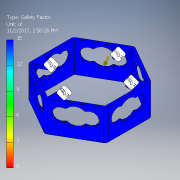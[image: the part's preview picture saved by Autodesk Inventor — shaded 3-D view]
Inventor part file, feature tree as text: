
AUTODESK INVENTOR PART (.ipt)
format: ipt  version: 2018 (Build 220112000, 112)  size: 514,048 bytes
history: native  units: mm
features: extrude x19, sketch x15, projected_geometry x14, fillet x2, hole x1, pattern_circular x1
ambient origin geometry x8: Origin, YZ Plane, XZ Plane, XY Plane, X Axis, Y Axis, Z Axis, Center Point
bodies: Solid1 (feature_tree)
feature tree (52):
  extrude  "Extrusion1"  Depth=3.0mm
  extrude  "Extrusion2"  Depth=37.0mm
  sketch  "Sketch5"  dims[d5=4.0mm d6=0.0mm d49=25.5mm]
  extrude  "Extrusion3"  Depth=4.0mm
  extrude  "Extrusion4"  Depth=11.7mm
  extrude  "Extrusion5"  Depth=23.0mm
  sketch  "Sketch9"  dims[d66=8.5mm d67=27.0mm]
  hole  "Hole3"  [1 undecoded]
  extrude  "Extrusion6"  Depth=27.0mm
  extrude  "Extrusion7"  Depth=22.0mm
  extrude  "Extrusion8"  Depth=13.0mm
  extrude  "Extrusion9"  Depth=14.5mm
  extrude  "Extrusion10"  Depth=54.864mm
  extrude  "Extrusion11"  Depth=4.5mm
  pattern_circular  "Circular Pattern1"  [2 undecoded]
  extrude  "Extrusion12"  Depth=22.0mm
  extrude  "Extrusion13"  Depth=22.0mm
  fillet  "Fillet1"  Radius=3.0mm
  fillet  "Fillet2"  Radius=3.0mm
  extrude  "Extrusion16"  Depth=3.0mm TaperAngle=0.0deg
  extrude  "Extrusion14"  Depth=3.0mm TaperAngle=0.0deg
  extrude  "Extrusion15"  Depth=3.0mm TaperAngle=0.0deg
  extrude  "Extrusion17"  Depth=3.0mm TaperAngle=0.0deg
  extrude  "Extrusion19"  Depth=4.0mm TaperAngle=360.0deg
  extrude  "Extrusion18"  Depth=10.0mm TaperAngle=0.0deg
  sketch  "Sketch1"  dims[d0=54.864mm d1=3.0mm]
  sketch  "Sketch2"  dims[d2=37.0mm d3=0.0mm d4=15.25mm]
  sketch  "Sketch6"  dims[d51=8.44mm d53=11.7mm]
  projected_geometry  "Projected Loop1"
  sketch  "Sketch7"  dims[d54=15.0mm d55=23.0mm]
  projected_geometry  "Projected Loop2"
  sketch  "Sketch8"  dims[d56=3.0mm d57=0.0mm d58=14.5mm]
  projected_geometry  "Projected Loop3"
  projected_geometry  "Projected Loop4"
  projected_geometry  "Projected Loop5"
  projected_geometry  "Projected Loop6"
  projected_geometry  "Projected Loop7"
  sketch  "Sketch10"  dims[d68=14.5mm d70=22.0mm]
  projected_geometry  "Projected Loop8"
  projected_geometry  "Projected Loop9"
  projected_geometry  "Projected Loop10"
  projected_geometry  "Projected Loop11"
  projected_geometry  "Projected Loop12"
  projected_geometry  "Projected Loop13"
  sketch  "Sketch11"  dims[d71=15.0mm d72=13.0mm]
  projected_geometry  "Projected Loop14"
  sketch  "Sketch12"  dims[d73=3.0mm d74=0.0mm]
  sketch  "Sketch13"  dims[d75=27.0mm d76=8.5mm d77=11.0mm d78=13.0mm d79=15.0mm d81=14.5mm]
  sketch  "Sketch14"  dims[d82=54.864mm d83=54.864mm]
  sketch  "Sketch15"  dims[d84=3.0mm d85=0.0mm]
  sketch  "Sketch16"  dims[d86=3.1mm d87=39.0mm d88=4.5mm d89=4.5mm d90=4.5mm d91=4.5mm d92=4.5mm d93=4.5mm d94=4.5mm d95=4.5mm d96=4.5mm d97=4.5mm d98=4.5mm]
  sketch  "Sketch17"  dims[d99=4.5mm d100=22.0mm d101=22.0mm d102=22.0mm d103=3.7mm d104=6.0mm d105=4.0mm d106=2.0mm d107=90.0deg d108=8.0mm d109=20.594885mm d110=3.0mm d111=0.0mm d112=3.0mm d113=0.0mm d114=3.0mm d115=0.0mm d116=3.0mm d117=0.0mm d118=3.0mm d119=0.0mm d120=3.0mm d121=0.0mm d122=60.0mm d123=360.0deg d125=10.0mm d126=0.0mm d127=10.0mm d128=0.0mm d129=4.0mm d130=4.0mm d131=0.4mm d132=0.0mm d133=0.4mm d134=0.0mm d135=0.4mm d136=0.0mm d137=0.4mm d138=0.0mm d139=0.4mm d140=0.0mm d141=0.4mm d142=0.0mm d29=1.0mm d30=1.0mm d143=1.0mm d144=1.0mm]
note: 3 required parameter values undecoded (feature->parameter linkage not recoverable at this tier; creation-order binding heuristic only, values carry confidence <= 0.55)
